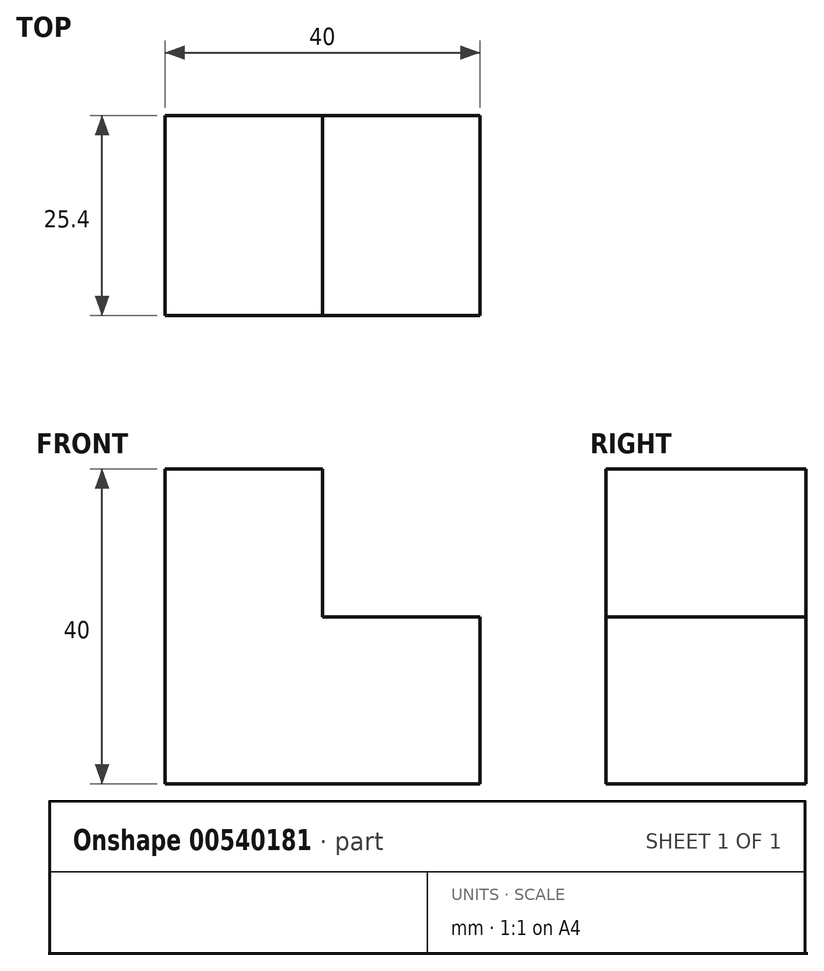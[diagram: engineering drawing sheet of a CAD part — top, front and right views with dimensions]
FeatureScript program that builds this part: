
annotation { "Feature Type Name" : "Feature", "Feature Type Description" : "" }
export const myFeature = defineFeature(function(context is Context, id is Id, definition is map)
    precondition{}
    {
        {
            var Q0;
            Q0=qCreatedBy(makeId("Front.planeOp"),FACE);
            var sketch = newSketch(context, id + "F0", { "sketchPlane" : qUnion([Q0])});
            skLineSegment(sketch, "E0", {"start": v(-35.04, 25.85) * mm, "end": v(-15.04, 25.85) * mm});
            skLineSegment(sketch, "E1", {"start": v(-35.04, 25.85) * mm, "end": v(-35.04, -14.15) * mm});
            skLineSegment(sketch, "E2", {"start": v(-35.04, -14.15) * mm, "end": v(4.96, -14.15) * mm});
            skLineSegment(sketch, "E3", {"start": v(4.96, -14.15) * mm, "end": v(4.96, 5.85) * mm});
            skLineSegment(sketch, "E4", {"start": v(-15.04, 25.85) * mm, "end": v(-15.04, 3.51) * mm});
            skLineSegment(sketch, "E5", {"start": v(-15.04, 3.51) * mm, "end": v(-15.04, 7.04) * mm});
            skLineSegment(sketch, "E6", {"start": v(-15.04, 7.04) * mm, "end": v(4.96, 7.04) * mm});
            skLineSegment(sketch, "E7", {"start": v(4.96, 5.85) * mm, "end": v(4.96, 7.04) * mm});
            skSolve(sketch);
        }
        {
            var Q0;
            Q0=makeQuery(id+"F0.imprint","IMPRINT",FACE,{"disambiguationData":[TD([[makeQuery(id+"F0.imprint","IMPRINT",EDGE,{"derivedFrom":sQuery(id+"F0.wireOp",EDGE,"E0")}),-1.0]])]});
            extrude(context, id + "F1", {"entities" : qUnion([Q0]), "depth" : 25.4 * mm, "offsetDistance" : 25.4 * mm});
        }
    });
